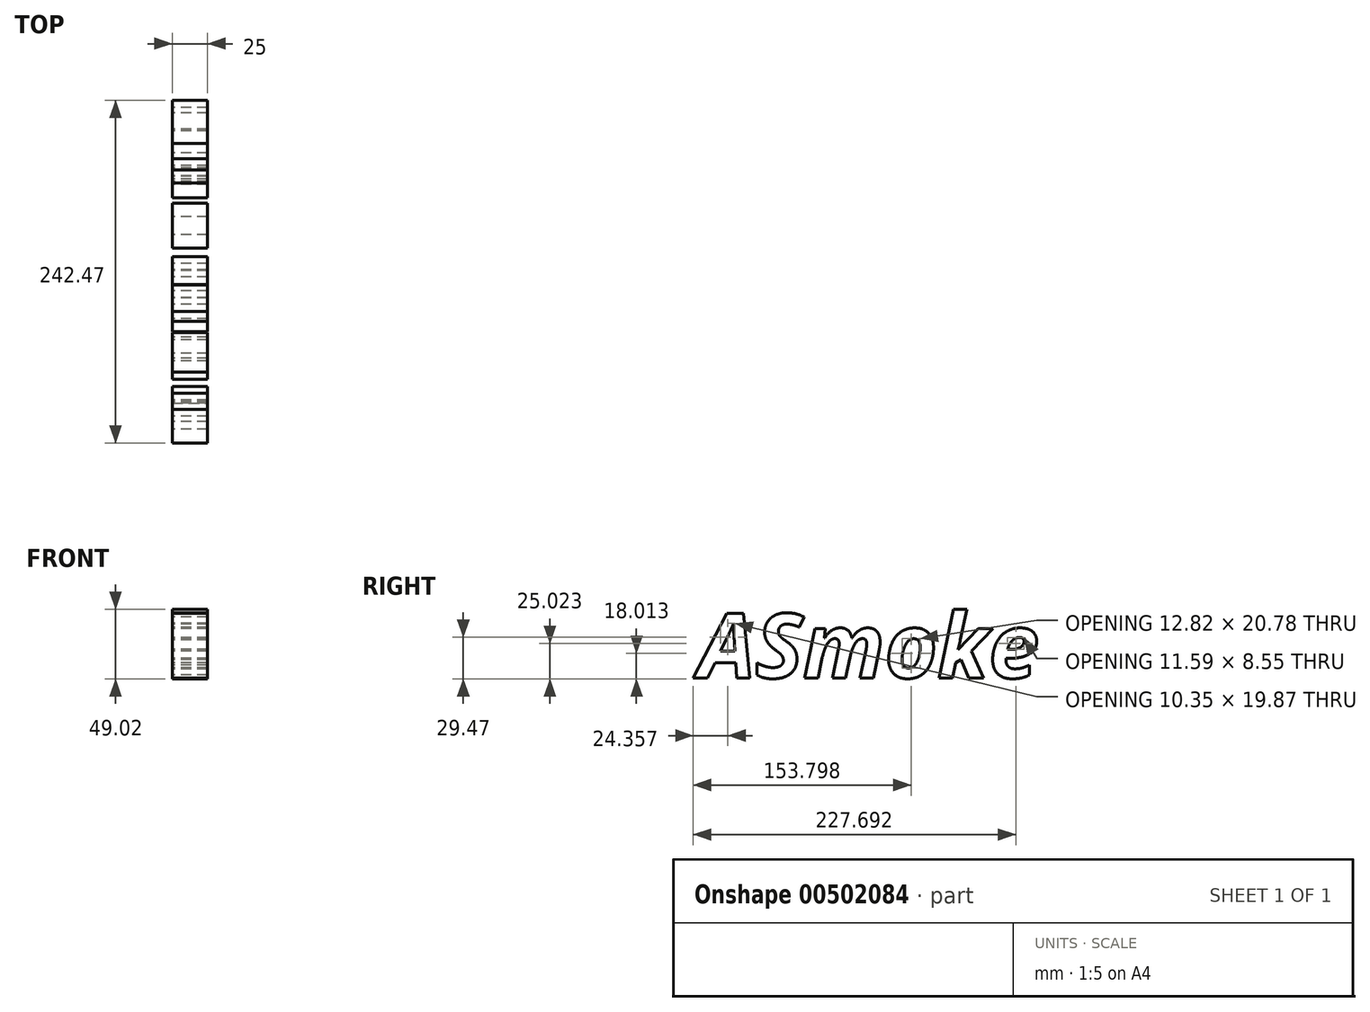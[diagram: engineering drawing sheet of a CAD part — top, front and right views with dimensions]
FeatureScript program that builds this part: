
annotation { "Feature Type Name" : "Feature", "Feature Type Description" : "" }
export const myFeature = defineFeature(function(context is Context, id is Id, definition is map)
    precondition{}
    {
        {
            var Q0;
            Q0=qCreatedBy(makeId("Right.planeOp"),FACE);
            var sketch = newSketch(context, id + "F0", { "sketchPlane" : qUnion([Q0])});
            skText(sketch, "E0", { "text": "ASmoke", "fontName": "OpenSans-BoldItalic.ttf"});
            const initialGuessF0  = {"E0": [-0.0832, -0.0075, 1, 0, 0.04585]};
            skSetInitialGuess(sketch, initialGuessF0);
            skSolve(sketch);
        }
        {
            var Q0;
            Q0 = qSketchRegion(id + "F0", true);
            extrude(context, id + "F1", {"entities" : qUnion([Q0]), "depth" : 25 * mm, "offsetDistance" : 25 * mm});
        }
    });
